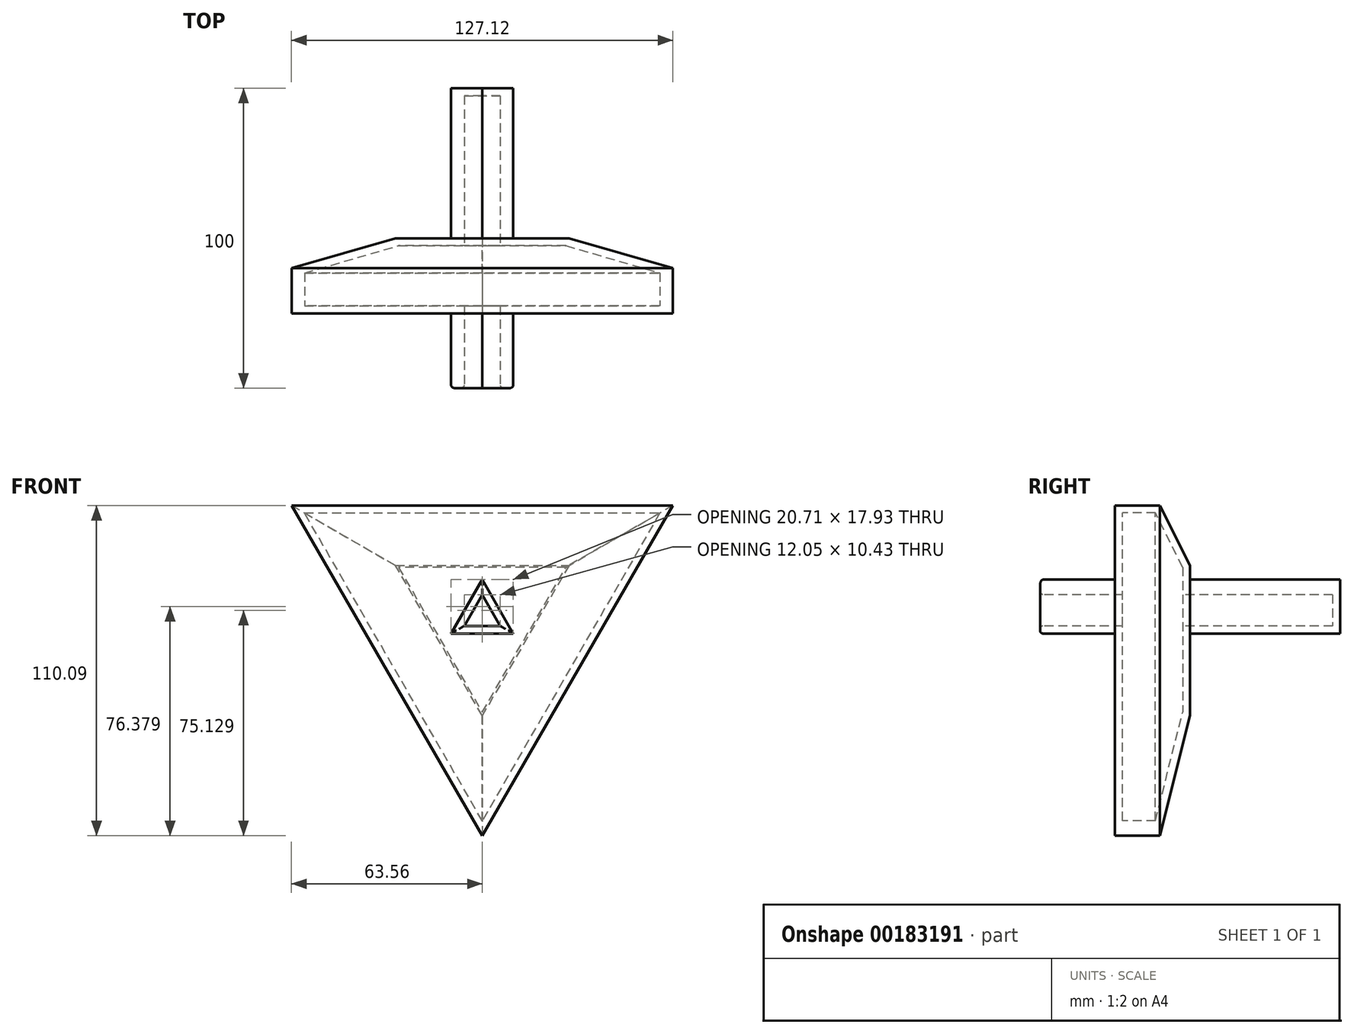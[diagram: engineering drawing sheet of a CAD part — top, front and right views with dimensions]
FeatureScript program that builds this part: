
annotation { "Feature Type Name" : "Feature", "Feature Type Description" : "" }
export const myFeature = defineFeature(function(context is Context, id is Id, definition is map)
    precondition{}
    {
        {
            var Q0;
            Q0=qCreatedBy(makeId("Front.planeOp"),FACE);
            var sketch = newSketch(context, id + "F0", { "sketchPlane" : qUnion([Q0])});
            skCircle(sketch, "E0.cCircle", {"center": v(0, 0) * mm, "radius": 36.7 * mm, "construction": true});
            skLineSegment(sketch, "E0.0", {"start": v(-63.56, 36.7) * mm, "end": v(63.56, 36.7) * mm});
            skLineSegment(sketch, "E0.1", {"start": v(63.56, 36.7) * mm, "end": v(0, -73.4) * mm});
            skLineSegment(sketch, "E0.2", {"start": v(0, -73.4) * mm, "end": v(-63.56, 36.7) * mm});
            skPoint(sketch, "E0.0.midPoint", {"position": v(0, 36.7) * mm});
            skSolve(sketch);
        }
        {
            var Q0;
            Q0=makeQuery(id+"F0.imprint","IMPRINT",FACE,{"disambiguationData":[TD([[makeQuery(id+"F0.imprint","IMPRINT",EDGE,{"derivedFrom":sQuery(id+"F0.wireOp",EDGE,"E0.0")}),-1.0]])]});
            extrude(context, id + "F1", {"entities" : qUnion([Q0]), "oppositeDirection" : true, "depth" : 25 * mm});
        }
        {
            var Q0;
            Q0=makeQuery(id+"F1.opExtrude","CAP_EDGE",EDGE,{"disambiguationData":[OSD([sQuery(id+"F0.wireOp",EDGE,"E0.2")])],"isStart":false});
            var Q1;
            Q1=makeQuery(id+"F1.opExtrude","CAP_EDGE",EDGE,{"disambiguationData":[OSD([sQuery(id+"F0.wireOp",EDGE,"E0.0")])],"isStart":false});
            var Q2;
            Q2=makeQuery(id+"F1.opExtrude","CAP_EDGE",EDGE,{"disambiguationData":[OSD([sQuery(id+"F0.wireOp",EDGE,"E0.1")])],"isStart":false});
            var Q3;
            Q3=makeQuery(id+"F1.opExtrude","CAP_FACE",FACE,{"disambiguationData":[OSD([sQuery(id+"F0.wireOp",EDGE,"E0.0"),sQuery(id+"F0.wireOp",EDGE,"E0.1"),sQuery(id+"F0.wireOp",EDGE,"E0.2")])],"isStart":false});
            chamfer(context, id + "F2", {"entities" : qUnion([Q0, Q1, Q2, Q3]), "chamferType" : ChamferType.TWO_OFFSETS, "width1" : 20 * mm, "oppositeDirection" : false, "width2" : 10 * mm});
        }
        {
            var Q0;
            Q0=makeQuery(id+"F1.opExtrude","CAP_FACE",FACE,{"disambiguationData":[OSD([sQuery(id+"F0.wireOp",EDGE,"E0.0"),sQuery(id+"F0.wireOp",EDGE,"E0.1"),sQuery(id+"F0.wireOp",EDGE,"E0.2")])],"isStart":false});
            var sketch = newSketch(context, id + "F3", { "sketchPlane" : qUnion([Q0])});
            skCircle(sketch, "E1.cCircle", {"center": v(0, 0) * mm, "radius": 5.98 * mm, "construction": true});
            skLineSegment(sketch, "E1.0", {"start": v(10.35, -5.98) * mm, "end": v(-10.35, -5.98) * mm});
            skLineSegment(sketch, "E1.1", {"start": v(-10.35, -5.98) * mm, "end": v(0, 11.96) * mm});
            skLineSegment(sketch, "E1.2", {"start": v(0, 11.96) * mm, "end": v(10.35, -5.98) * mm});
            skPoint(sketch, "E1.0.midPoint", {"position": v(0, -5.98) * mm});
            skPoint(sketch, "E2", {"position": v(0, 16.7) * mm});
            skSolve(sketch);
        }
        {
            var Q0;
            Q0 = qSketchRegion(id + "F3", true);
            extrude(context, id + "F4", {"entities" : qUnion([Q0]), "operationType" : NewBodyOperationType.ADD, "endBound" : BoundingType.SYMMETRIC, "depth" : 100 * mm});
        }
        {
            var Q0;
            Q0=makeQuery(id+"F4.opExtrude","CAP_FACE",FACE,{"disambiguationData":[OSD([sQuery(id+"F3.wireOp",EDGE,"E1.0"),sQuery(id+"F3.wireOp",EDGE,"E1.1"),sQuery(id+"F3.wireOp",EDGE,"E1.2")])],"isStart":true});
            shell(context, id + "F5", {"entities" : qUnion([Q0]), "thickness" : 2.5 * mm});
        }
        {
            var Q0;
            Q0=makeQuery(id+"F4.opExtrude","CAP_EDGE",EDGE,{"disambiguationData":[OSD([sQuery(id+"F3.wireOp",EDGE,"E1.0")])],"isStart":true});
            var Q1;
            {var subQ0=sQuery(id+"F3.wireOp",EDGE,"E1.0");Q1=makeQuery(id+"F5.opShell","OFFSET_EDGE",EDGE,{"disambiguationData":[OSD([subQ0]),TDD([makeQuery(id+"F4.opExtrude","CAP_EDGE",EDGE,{"disambiguationData":[OSD([subQ0])],"isStart":true})])]});}
            var Q2;
            {var subQ0=sQuery(id+"F3.wireOp",EDGE,"E1.1");Q2=makeQuery(id+"F5.opShell","OFFSET_EDGE",EDGE,{"disambiguationData":[OSD([subQ0]),TDD([makeQuery(id+"F4.opExtrude","CAP_EDGE",EDGE,{"disambiguationData":[OSD([subQ0])],"isStart":true})])]});}
            var Q3;
            Q3=makeQuery(id+"F4.opExtrude","CAP_EDGE",EDGE,{"disambiguationData":[OSD([sQuery(id+"F3.wireOp",EDGE,"E1.1")])],"isStart":true});
            var Q4;
            Q4=makeQuery(id+"F4.opExtrude","CAP_EDGE",EDGE,{"disambiguationData":[OSD([sQuery(id+"F3.wireOp",EDGE,"E1.2")])],"isStart":true});
            var Q5;
            {var subQ0=sQuery(id+"F3.wireOp",EDGE,"E1.2");Q5=makeQuery(id+"F5.opShell","OFFSET_EDGE",EDGE,{"disambiguationData":[OSD([subQ0]),TDD([makeQuery(id+"F4.opExtrude","CAP_EDGE",EDGE,{"disambiguationData":[OSD([subQ0])],"isStart":true})])]});}
            fillet(context, id + "F6", {"entities" : qUnion([Q0, Q1, Q2, Q3, Q4, Q5]), "radius" : 1 * mm, "tangentPropagation" : true, "allowEdgeOverflow" : false});
        }
    });
